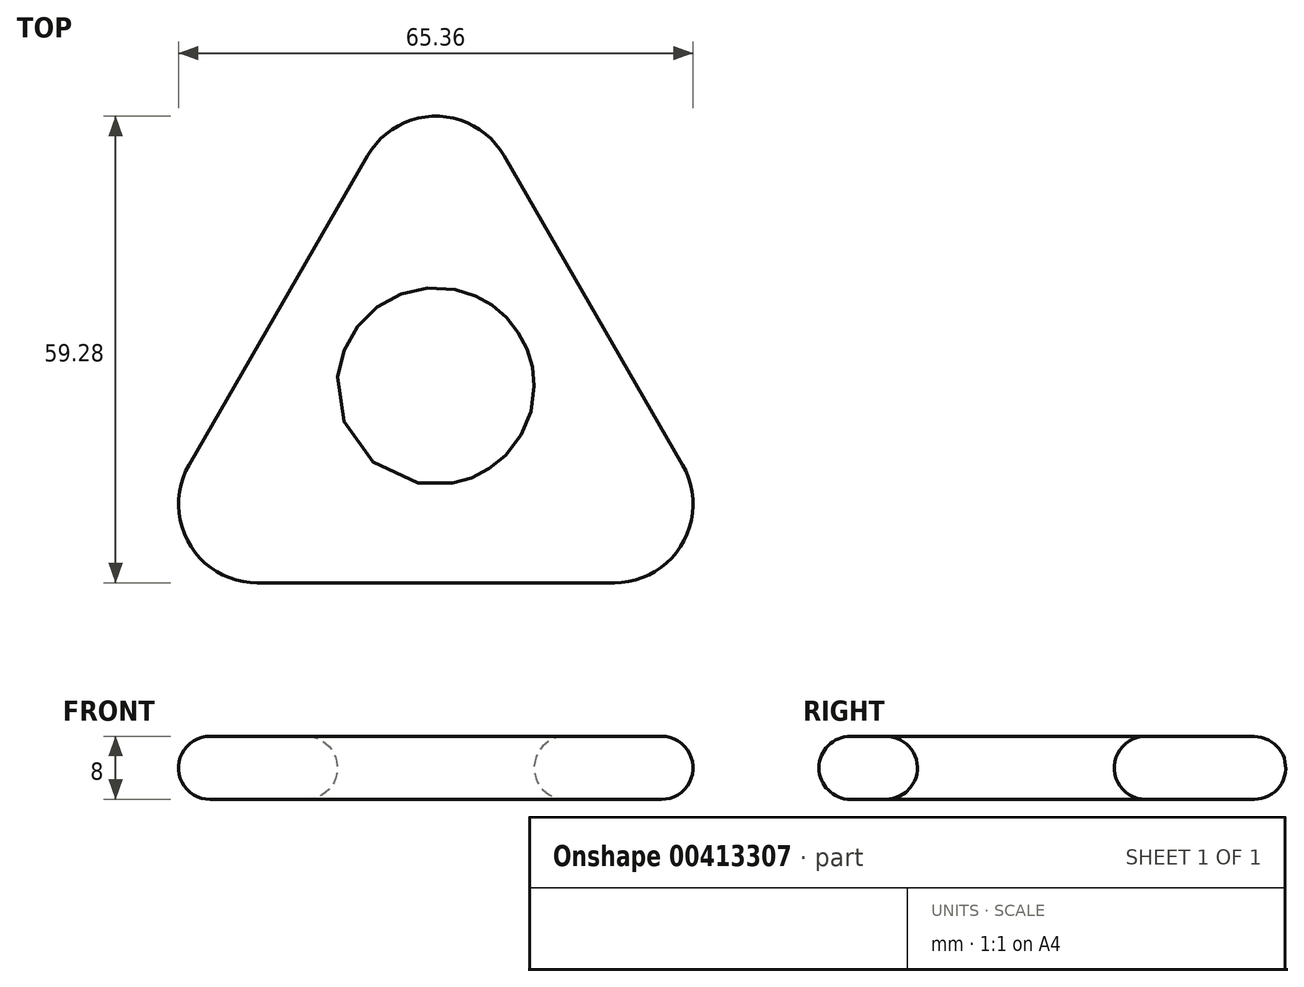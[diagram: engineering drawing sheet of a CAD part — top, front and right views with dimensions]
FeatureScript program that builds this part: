
annotation { "Feature Type Name" : "Feature", "Feature Type Description" : "" }
export const myFeature = defineFeature(function(context is Context, id is Id, definition is map)
    precondition{}
    {
        {
            var Q0;
            Q0=qCreatedBy(makeId("Top.planeOp"),FACE);
            var sketch = newSketch(context, id + "F0", { "sketchPlane" : qUnion([Q0])});
            skLineSegment(sketch, "E0", {"start": v(0, 44.28) * mm, "end": v(-40, -25) * mm});
            skLineSegment(sketch, "E1", {"start": v(-40, -25) * mm, "end": v(40, -25) * mm});
            skLineSegment(sketch, "E2", {"start": v(40, -25) * mm, "end": v(0, 44.28) * mm});
            skCircle(sketch, "E3", {"center": v(0, 0) * mm, "radius": 12.5 * mm});
            skLineSegment(sketch, "E4", {"start": v(0, 0) * mm, "end": v(0, -25) * mm});
            skSolve(sketch);
        }
        {
            var Q0;
            {var subQ3=sQuery(id+"F0.wireOp",EDGE,"E0");Q0=makeQuery(id+"F0.imprint","IMPRINT",FACE,{"disambiguationData":[TD([[makeQuery(id+"F0.imprint","IMPRINT",EDGE,{"derivedFrom":subQ3}),1.0]])]});}
            extrude(context, id + "F1", {"entities" : qUnion([Q0]), "depth" : 4 * mm});
        }
        {
            var Q0;
            Q0=makeQuery(id+"F1.opExtrude","SWEPT_EDGE",EDGE,{"disambiguationData":[OSD([sQuery(id+"F0.wireOp",EDGE,"E0"),sQuery(id+"F0.wireOp",EDGE,"E2")])]});
            var Q1;
            Q1=makeQuery(id+"F1.opExtrude","SWEPT_EDGE",EDGE,{"disambiguationData":[OSD([sQuery(id+"F0.wireOp",EDGE,"E0"),sQuery(id+"F0.wireOp",EDGE,"E1")])]});
            var Q2;
            Q2=makeQuery(id+"F1.opExtrude","SWEPT_EDGE",EDGE,{"disambiguationData":[OSD([sQuery(id+"F0.wireOp",EDGE,"E1"),sQuery(id+"F0.wireOp",EDGE,"E2")])]});
            fillet(context, id + "F2", {"entities" : qUnion([Q0, Q1, Q2]), "radius" : 10 * mm, "tangentPropagation" : true, "allowEdgeOverflow" : false});
        }
        {
            var Q0;
            Q0=makeQuery(id+"F1.opExtrude","CAP_EDGE",EDGE,{"disambiguationData":[OSD([sQuery(id+"F0.wireOp",EDGE,"E3")])],"isStart":false});
            var Q1;
            Q1=makeQuery(id+"F1.opExtrude","CAP_EDGE",EDGE,{"disambiguationData":[OSD([sQuery(id+"F0.wireOp",EDGE,"E2")])],"isStart":false});
            fillet(context, id + "F3", {"entities" : qUnion([Q0, Q1]), "radius" : 4 * mm, "tangentPropagation" : true, "allowEdgeOverflow" : false});
        }
        {
            var Q0;
            Q0=makeQuery(id+"F1.opExtrude","SWEPT_BODY",BODY,{"disambiguationData":[OSD([sQuery(id+"F0.wireOp",EDGE,"E0"),sQuery(id+"F0.wireOp",EDGE,"E1"),sQuery(id+"F0.wireOp",EDGE,"E2"),sQuery(id+"F0.wireOp",EDGE,"E3")])]});
            var Q1;
            Q1=qCreatedBy(makeId("Top.planeOp"),FACE);
            mirror(context, id + "F4", {"operationType" : NewBodyOperationType.ADD, "entities" : qUnion([Q0]), "mirrorPlane" : qUnion([Q1])});
        }
    });
